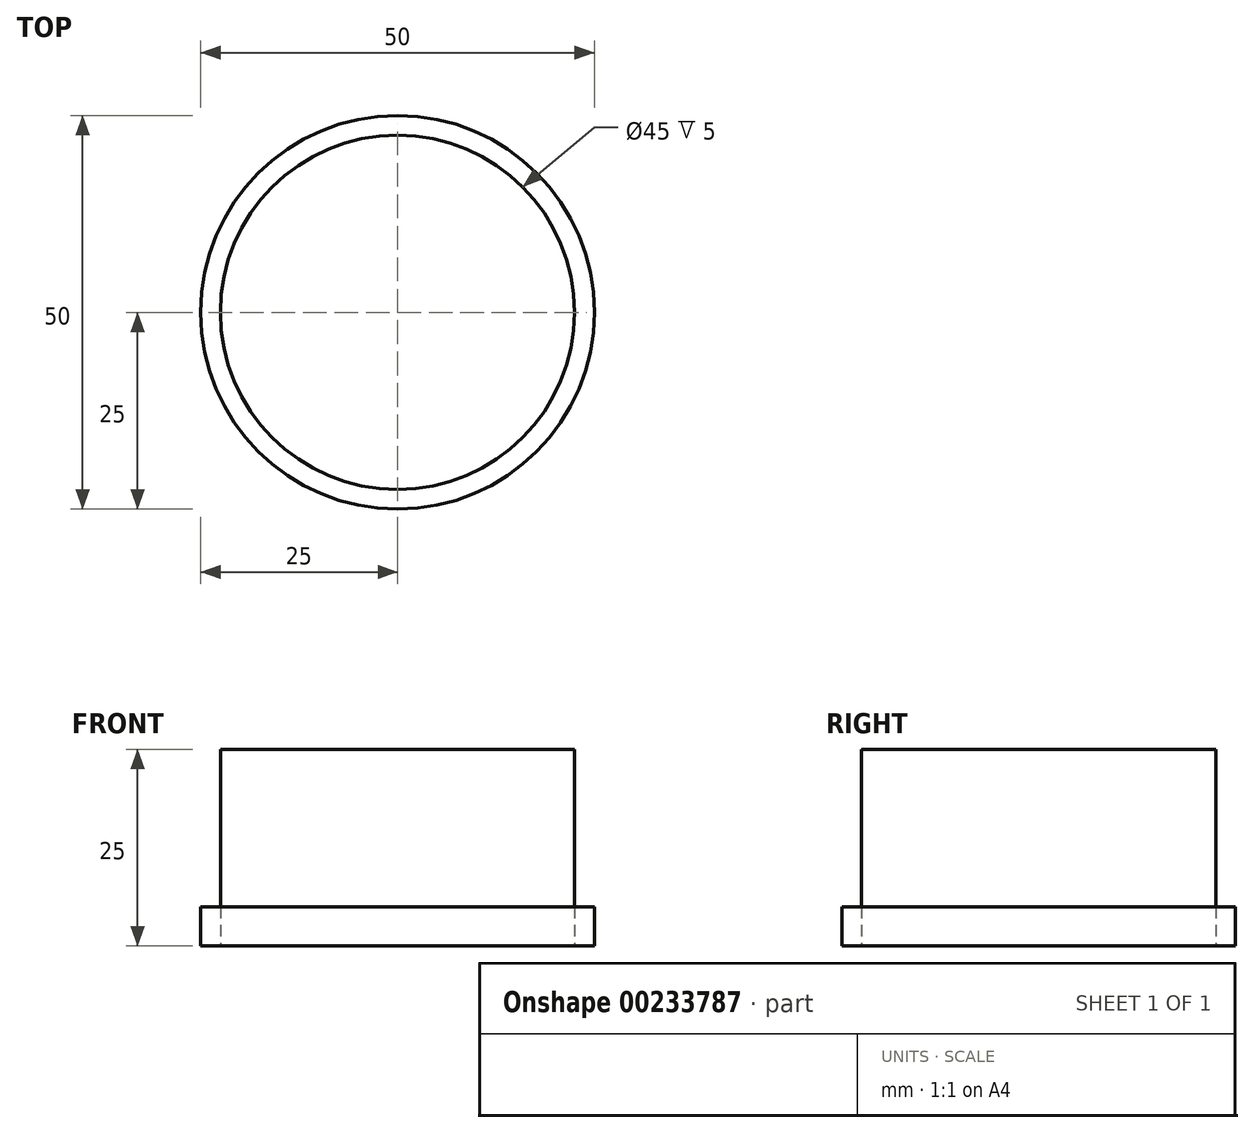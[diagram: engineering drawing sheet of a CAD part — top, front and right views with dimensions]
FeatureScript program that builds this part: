
annotation { "Feature Type Name" : "Feature", "Feature Type Description" : "" }
export const myFeature = defineFeature(function(context is Context, id is Id, definition is map)
    precondition{}
    {
        {
            var Q0;
            Q0=qCreatedBy(makeId("Top.planeOp"),FACE);
            var sketch = newSketch(context, id + "F0", { "sketchPlane" : qUnion([Q0])});
            skCircle(sketch, "E0", {"center": v(0, 0) * mm, "radius": 22.5 * mm});
            skSolve(sketch);
        }
        {
            var Q0;
            Q0 = qSketchRegion(id + "F0", true);
            extrude(context, id + "F1", {"entities" : qUnion([Q0]), "depth" : 25 * mm});
        }
        {
            var Q0;
            Q0=makeQuery(id+"F1.opExtrude","CAP_FACE",FACE,{"disambiguationData":[OSD([sQuery(id+"F0.wireOp",EDGE,"E0")])],"isStart":true});
            var sketch = newSketch(context, id + "F2", { "sketchPlane" : qUnion([Q0])});
            skCircle(sketch, "E1.0", {"center": v(0, 0) * mm, "radius": 22.5 * mm});
            skCircle(sketch, "E2", {"center": v(0, 0) * mm, "radius": 25 * mm});
            skSolve(sketch);
        }
        {
            var Q0;
            Q0 = qSketchRegion(id + "F2", true);
            extrude(context, id + "F3", {"entities" : qUnion([Q0]), "oppositeDirection" : true, "depth" : 5 * mm});
        }
    });
